# Revit family: Комплект садовой мебели «Поло» Арт 18869
name_source: partatom
category: Антураж
revit_build: Autodesk Revit 2018 (Build: 20180423_1000(x64)
units: mm (PartAtom-declared; Revit-internal decimal feet)

## family parameters
Всегда вертикально = Да
Источник визуального образа = Геометрия семейства
На основе рабочей плоскости = Нет
Общий = Нет
При загрузке вырезать с полостями = Нет
Точка расчета площади = Нет

## types (2) — shared parameters
URL = https://hobbyka.ru
Артикул товара = Арт. 18869
Группа модели = Комплекты садовой мебели
Изготовитель = ООО «Хоббика».
Изображение типоразмера = Комплект садовой мебели «Поло» Арт 18869.jpg
Материал изделия = Сталь, дерево

## per-type parameters (varying)
| type | Высота | Длина | Лавка | Стол | Ширина |
| Комплект садовой мебели «Поло». Стол | 720 мм | 1500 мм | Нет | Да | 700 мм |
| Комплект садовой мебели «Поло». Лавка | 440 мм | 1200 мм | Да | Нет | 450 мм |

note: column(s) folded — value = type name in every type: Описание
